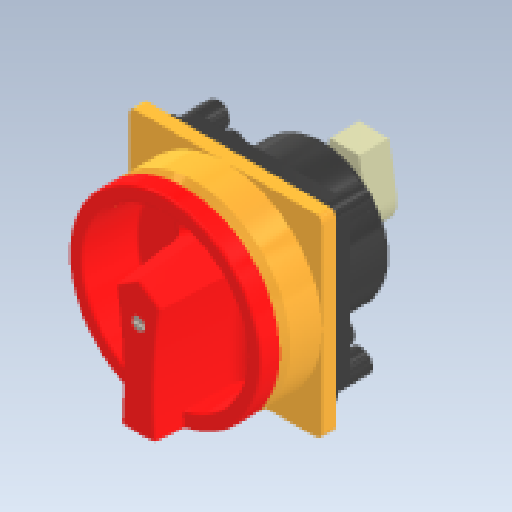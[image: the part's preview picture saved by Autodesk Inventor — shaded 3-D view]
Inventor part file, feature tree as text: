
AUTODESK INVENTOR PART (.ipt)
format: ipt  version: 2025.2 (Build 292293000, 293)  size: 701,440 bytes
history: native  units: mm
features: other x5, fillet x2, chamfer x1
ambient origin geometry x8: Origin, YZ Plane, XZ Plane, XY Plane, X Axis, Y Axis, Z Axis, Center Point
bodies: Body1 (feature_tree), Body2 (feature_tree), Body3 (feature_tree), Body4 (feature_tree)
feature tree (8):
  other  "Sólido1"
  other  "Sólido2"
  other  "Sólido3"
  other  "Sólido4"
  fillet  "Fillet3"  [1 undecoded]
  fillet  "Fillet4"  [1 undecoded]
  chamfer  "Chamfer1"  [1 undecoded]
  other  "Move Face1"
note: 3 required parameter values undecoded (feature->parameter linkage not recoverable at this tier; creation-order binding heuristic only, values carry confidence <= 0.55)
